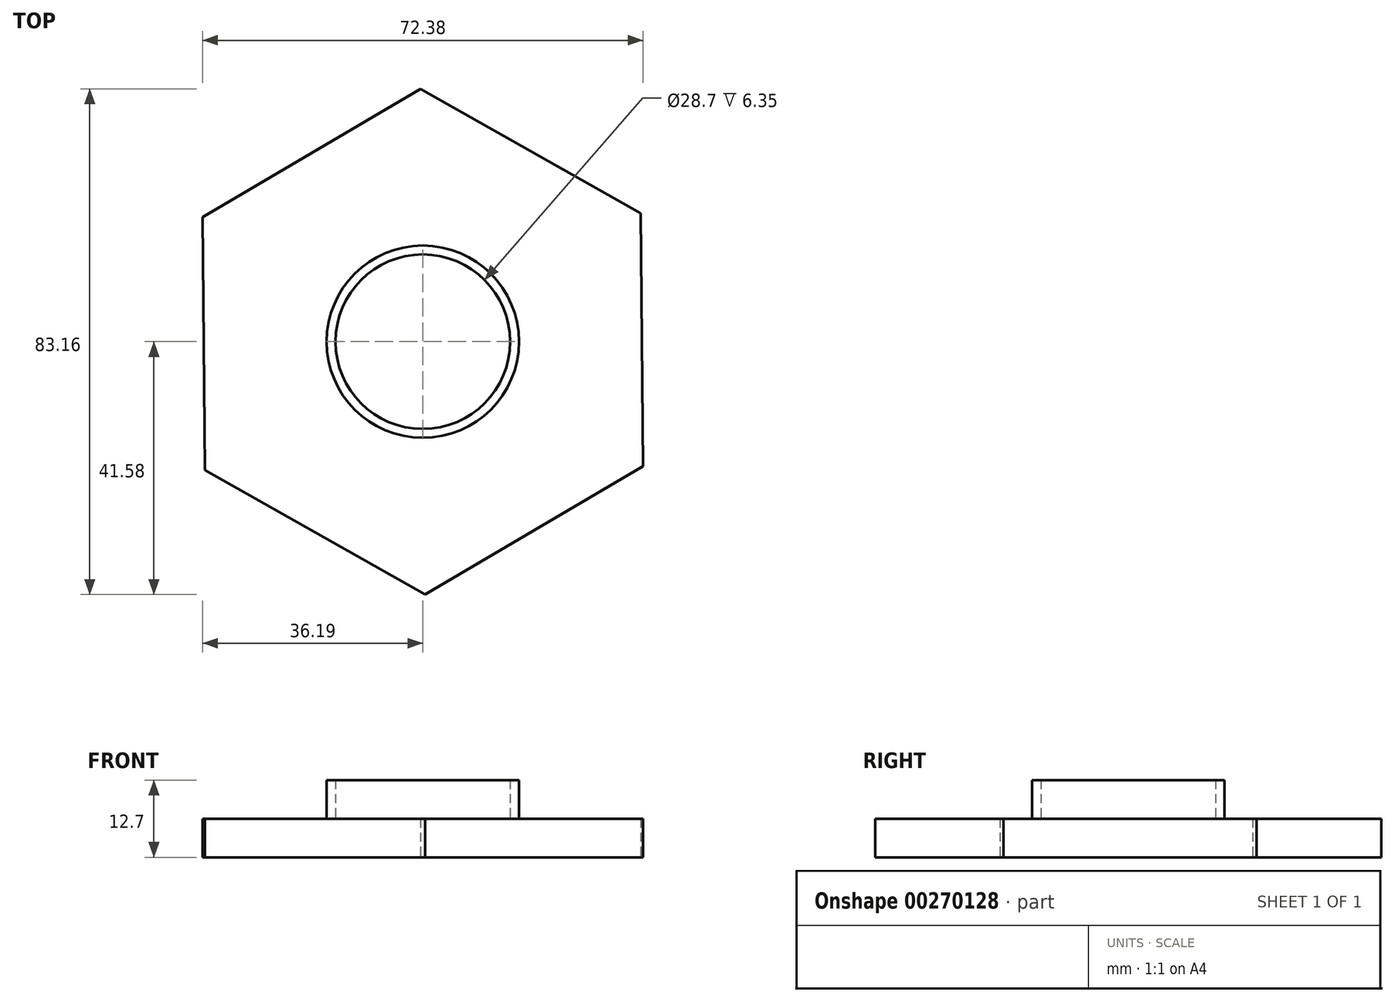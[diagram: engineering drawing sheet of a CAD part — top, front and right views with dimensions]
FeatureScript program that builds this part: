
annotation { "Feature Type Name" : "Feature", "Feature Type Description" : "" }
export const myFeature = defineFeature(function(context is Context, id is Id, definition is map)
    precondition{}
    {
        {
            var Q0;
            Q0=qCreatedBy(makeId("Top.planeOp"),FACE);
            var sketch = newSketch(context, id + "F0", { "sketchPlane" : qUnion([Q0])});
            skCircle(sketch, "E0.cCircle", {"center": v(0, 0) * mm, "radius": 36.01 * mm, "construction": true});
            skLineSegment(sketch, "E0.0", {"start": v(36.2, -20.48) * mm, "end": v(0.36, -41.58) * mm});
            skLineSegment(sketch, "E0.1", {"start": v(0.36, -41.58) * mm, "end": v(-35.83, -21.1) * mm});
            skLineSegment(sketch, "E0.2", {"start": v(-35.83, -21.1) * mm, "end": v(-36.2, 20.48) * mm});
            skLineSegment(sketch, "E0.3", {"start": v(-36.2, 20.48) * mm, "end": v(-0.36, 41.58) * mm});
            skLineSegment(sketch, "E0.4", {"start": v(-0.36, 41.58) * mm, "end": v(35.83, 21.1) * mm});
            skLineSegment(sketch, "E0.5", {"start": v(35.83, 21.1) * mm, "end": v(36.2, -20.48) * mm});
            skPoint(sketch, "E0.0.midPoint", {"position": v(18.28, -31.03) * mm});
            skSolve(sketch);
        }
        {
            var Q0;
            Q0=makeQuery(id+"F0.imprint","IMPRINT",FACE,{"disambiguationData":[TD([[makeQuery(id+"F0.imprint","IMPRINT",EDGE,{"derivedFrom":sQuery(id+"F0.wireOp",EDGE,"E0.0")}),-1.0]])]});
            extrude(context, id + "F1", {"entities" : qUnion([Q0]), "depth" : 6.35 * mm});
        }
        {
            var Q0;
            Q0=makeQuery(id+"F1.opExtrude","CAP_FACE",FACE,{"disambiguationData":[OSD([sQuery(id+"F0.wireOp",EDGE,"E0.0"),sQuery(id+"F0.wireOp",EDGE,"E0.1"),sQuery(id+"F0.wireOp",EDGE,"E0.2"),sQuery(id+"F0.wireOp",EDGE,"E0.3"),sQuery(id+"F0.wireOp",EDGE,"E0.4"),sQuery(id+"F0.wireOp",EDGE,"E0.5")])],"isStart":false});
            var sketch = newSketch(context, id + "F2", { "sketchPlane" : qUnion([Q0])});
            skCircle(sketch, "E1", {"center": v(0, 0) * mm, "radius": 14.35 * mm});
            skCircle(sketch, "E2", {"center": v(0, 0) * mm, "radius": 15.81 * mm});
            skSolve(sketch);
        }
        {
            var Q0;
            Q0=makeQuery(id+"F2.imprint","IMPRINT",FACE,{"disambiguationData":[TD([[makeQuery(id+"F2.imprint","IMPRINT",EDGE,{"derivedFrom":sQuery(id+"F2.wireOp",EDGE,"E1")}),-1.0]])]});
            extrude(context, id + "F3", {"entities" : qUnion([Q0]), "operationType" : NewBodyOperationType.ADD, "depth" : 6.35 * mm});
        }
    });
